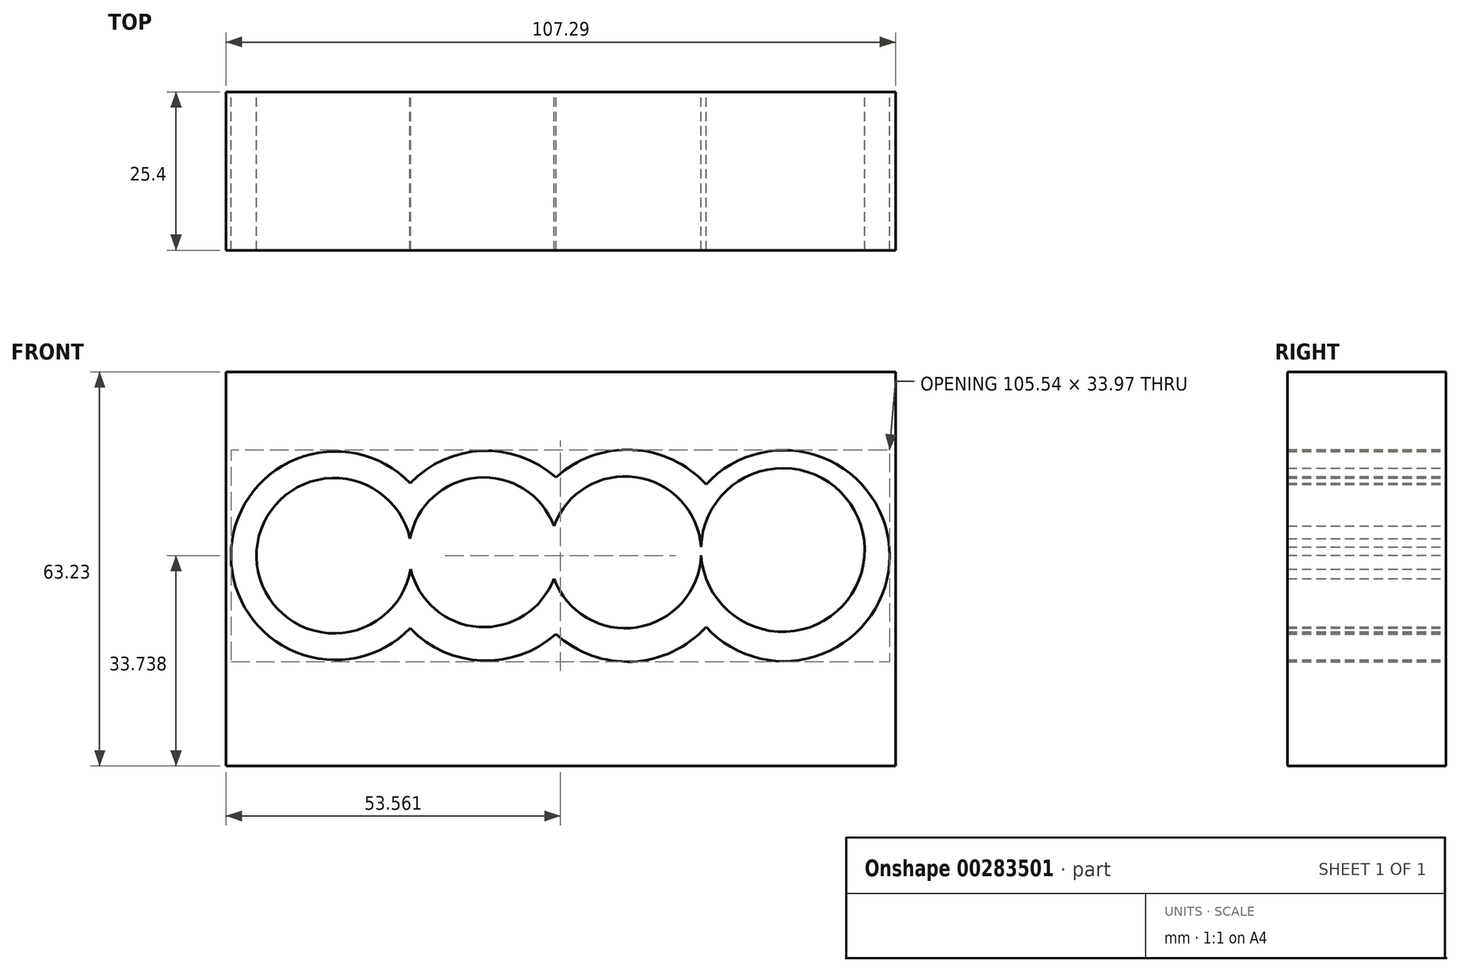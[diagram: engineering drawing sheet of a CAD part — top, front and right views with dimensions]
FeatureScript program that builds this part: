
annotation { "Feature Type Name" : "Feature", "Feature Type Description" : "" }
export const myFeature = defineFeature(function(context is Context, id is Id, definition is map)
    precondition{}
    {
        {
            var Q0;
            Q0=qCreatedBy(makeId("Front.planeOp"),FACE);
            var sketch = newSketch(context, id + "F0", { "sketchPlane" : qUnion([Q0])});
            skLineSegment(sketch, "E0.bottom", {"start": v(-54.38, 31.52) * mm, "end": v(52.9, 31.52) * mm});
            skLineSegment(sketch, "E0.top", {"start": v(-54.38, -31.7) * mm, "end": v(52.9, -31.7) * mm});
            skLineSegment(sketch, "E0.left", {"start": v(-54.38, 31.52) * mm, "end": v(-54.38, -31.7) * mm});
            skLineSegment(sketch, "E0.right", {"start": v(52.9, 31.52) * mm, "end": v(52.9, -31.7) * mm});
            skCircle(sketch, "E1", {"center": v(-36.87, 2.03) * mm, "radius": 16.72 * mm});
            skCircle(sketch, "E2", {"center": v(-12.72, 2.03) * mm, "radius": 16.83 * mm});
            skCircle(sketch, "E3", {"center": v(9.96, 2.03) * mm, "radius": 17 * mm});
            skCircle(sketch, "E4", {"center": v(35.03, 2.03) * mm, "radius": 16.92 * mm});
            skSolve(sketch);
        }
        {
            var Q0;
            Q0=makeQuery(id+"F0.imprint","IMPRINT",FACE,{"disambiguationData":[TD([[makeQuery(id+"F0.imprint","IMPRINT",EDGE,{"derivedFrom":sQuery(id+"F0.wireOp",EDGE,"E0.bottom")}),-1.0]])]});
            extrude(context, id + "F1", {"entities" : qUnion([Q0]), "depth" : 25.4 * mm});
        }
        {
            var Q0;
            Q0=qCreatedBy(makeId("Front.planeOp"),FACE);
            var sketch = newSketch(context, id + "F2", { "sketchPlane" : qUnion([Q0])});
            skCircle(sketch, "E5", {"center": v(-37.06, 2.03) * mm, "radius": 12.45 * mm});
            skCircle(sketch, "E6", {"center": v(-13.09, 2.58) * mm, "radius": 12 * mm});
            skCircle(sketch, "E7", {"center": v(9.59, 2.58) * mm, "radius": 12.17 * mm});
            skSolve(sketch);
        }
        {
            var Q0;
            Q0 = qSketchRegion(id + "F2", true);
            extrude(context, id + "F3", {"entities" : qUnion([Q0]), "depth" : 25.4 * mm});
        }
        {
            var Q0;
            Q0=qCreatedBy(makeId("Front.planeOp"),FACE);
            var sketch = newSketch(context, id + "F4", { "sketchPlane" : qUnion([Q0])});
            skCircle(sketch, "E8", {"center": v(34.84, 2.95) * mm, "radius": 13.12 * mm});
            skSolve(sketch);
        }
        {
            var Q0;
            Q0 = qSketchRegion(id + "F4", true);
            extrude(context, id + "F5", {"entities" : qUnion([Q0]), "operationType" : NewBodyOperationType.ADD, "depth" : 25.4 * mm});
        }
    });
